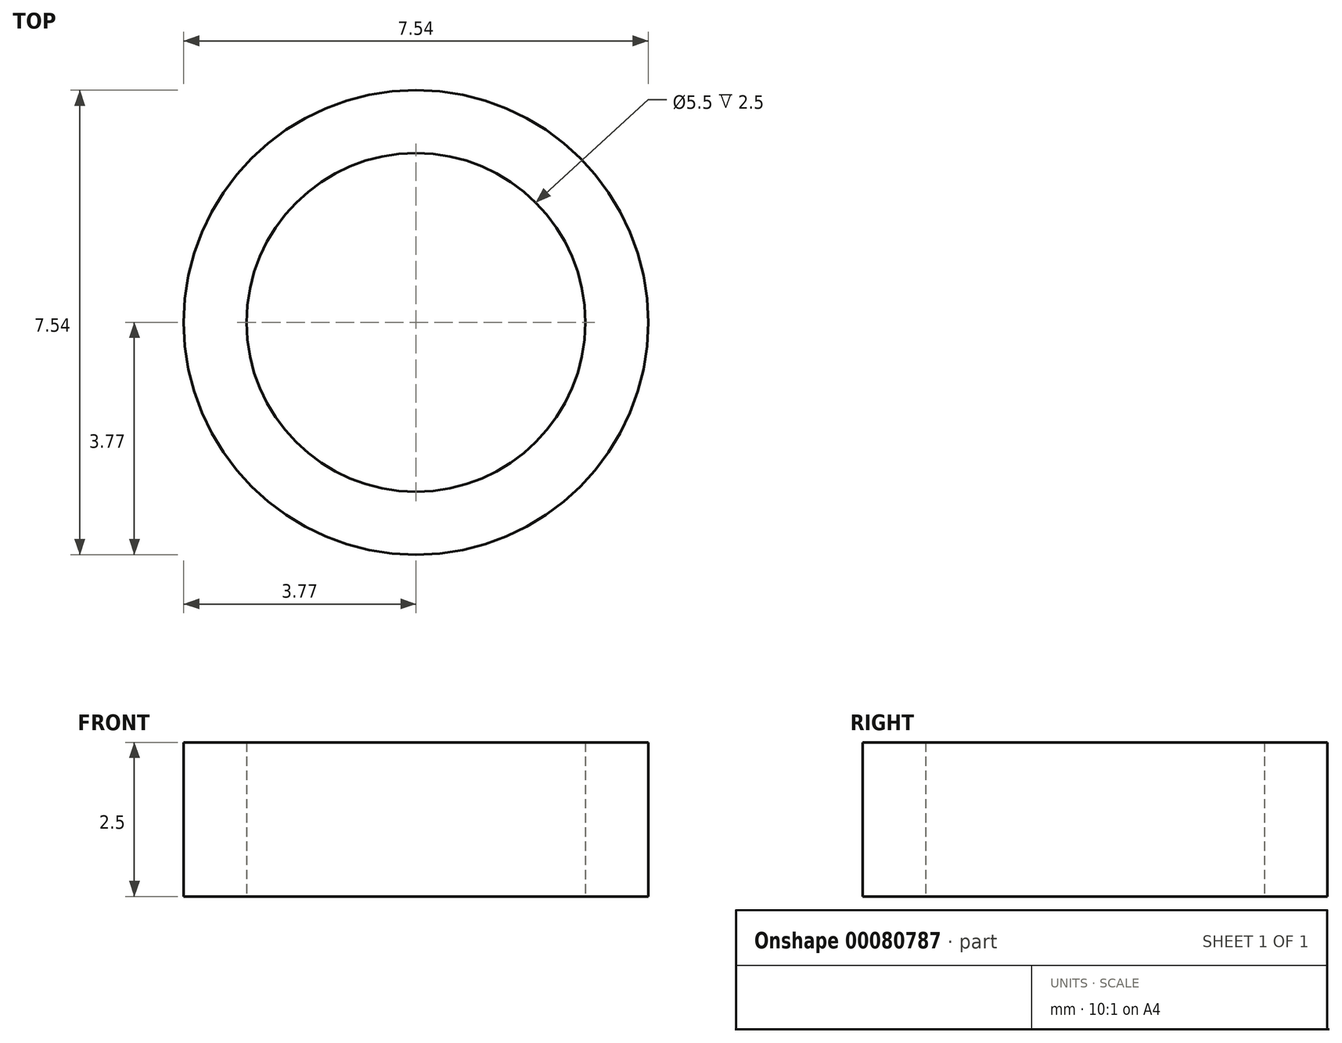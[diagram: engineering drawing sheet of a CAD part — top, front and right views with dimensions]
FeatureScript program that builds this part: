
annotation { "Feature Type Name" : "Feature", "Feature Type Description" : "" }
export const myFeature = defineFeature(function(context is Context, id is Id, definition is map)
    precondition{}
    {
        {
            var Q0;
            Q0=qCreatedBy(makeId("Top.planeOp"),FACE);
            var sketch = newSketch(context, id + "F0", { "sketchPlane" : qUnion([Q0])});
            skCircle(sketch, "E0", {"center": v(0, 0) * mm, "radius": 3.77 * mm});
            skCircle(sketch, "E1", {"center": v(0, 0) * mm, "radius": 2.75 * mm});
            skSolve(sketch);
        }
        {
            var Q0;
            Q0 = qSketchRegion(id + "F0", true);
            extrude(context, id + "F1", {"entities" : qUnion([Q0]), "depth" : 2.5 * mm});
        }
    });
